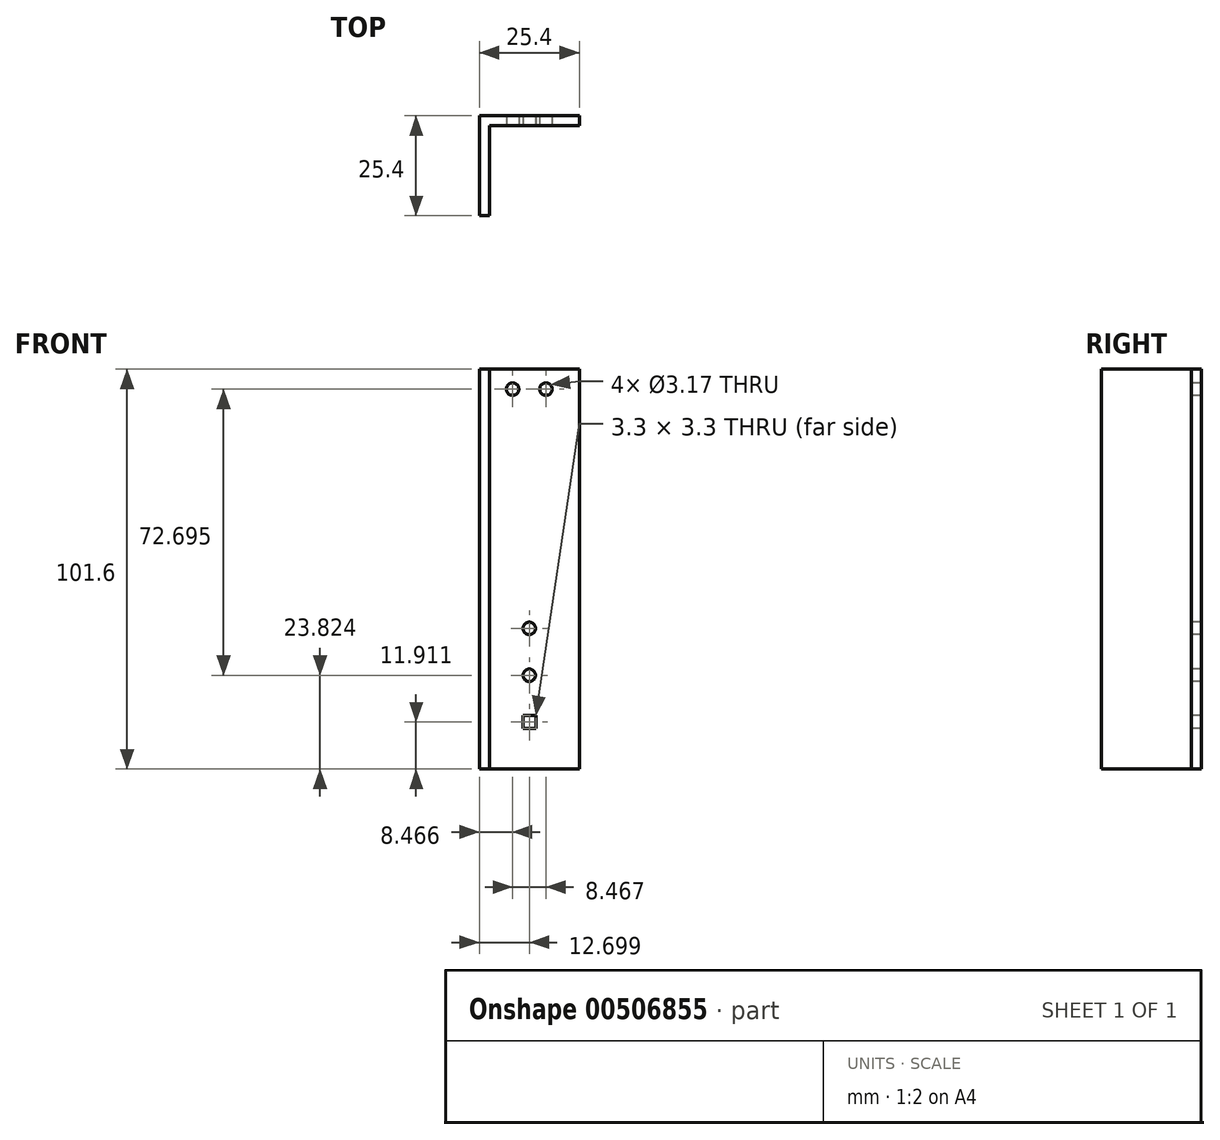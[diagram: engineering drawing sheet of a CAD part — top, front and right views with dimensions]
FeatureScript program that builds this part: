
annotation { "Feature Type Name" : "Feature", "Feature Type Description" : "" }
export const myFeature = defineFeature(function(context is Context, id is Id, definition is map)
    precondition{}
    {
        {
            var Q0;
            Q0=qCreatedBy(makeId("Front.planeOp"),FACE);
            var sketch = newSketch(context, id + "F0", { "sketchPlane" : qUnion([Q0])});
            skLineSegment(sketch, "E0.bottom", {"start": v(-30.83, 28.66) * mm, "end": v(-5.43, 28.66) * mm});
            skLineSegment(sketch, "E0.top", {"start": v(-30.83, -72.94) * mm, "end": v(-5.43, -72.94) * mm});
            skLineSegment(sketch, "E0.left", {"start": v(-30.83, 28.66) * mm, "end": v(-30.83, -72.94) * mm});
            skLineSegment(sketch, "E0.right", {"start": v(-5.43, 28.66) * mm, "end": v(-5.43, -72.94) * mm});
            skSolve(sketch);
        }
        {
            var Q0;
            Q0=makeQuery(id+"F0.imprint","IMPRINT",FACE,{"disambiguationData":[TD([[makeQuery(id+"F0.imprint","IMPRINT",EDGE,{"derivedFrom":sQuery(id+"F0.wireOp",EDGE,"E0.bottom")}),-1.0]])]});
            extrude(context, id + "F1", {"entities" : qUnion([Q0]), "depth" : 25.4 * mm, "offsetDistance" : 25.4 * mm});
        }
        {
            var Q0;
            Q0=makeQuery(id+"F1.opExtrude","SWEPT_FACE",FACE,{"disambiguationData":[OSD([sQuery(id+"F0.wireOp",EDGE,"E0.right")])]});
            var Q1;
            Q1=makeQuery(id+"F1.opExtrude","CAP_FACE",FACE,{"disambiguationData":[OSD([sQuery(id+"F0.wireOp",EDGE,"E0.bottom"),sQuery(id+"F0.wireOp",EDGE,"E0.top"),sQuery(id+"F0.wireOp",EDGE,"E0.left"),sQuery(id+"F0.wireOp",EDGE,"E0.right")])],"isStart":false});
            var Q2;
            Q2=makeQuery(id+"F1.opExtrude","SWEPT_FACE",FACE,{"disambiguationData":[OSD([sQuery(id+"F0.wireOp",EDGE,"E0.bottom")])]});
            var Q3;
            Q3=makeQuery(id+"F1.opExtrude","SWEPT_FACE",FACE,{"disambiguationData":[OSD([sQuery(id+"F0.wireOp",EDGE,"E0.top")])]});
            shell(context, id + "F2", {"entities" : qUnion([Q0, Q1, Q2, Q3]), "thickness" : 2.54 * mm});
        }
        {
            var Q0;
            Q0=makeQuery(id+"F2.opShell","OFFSET_FACE",FACE,{"disambiguationData":[OSD([sQuery(id+"F0.wireOp",EDGE,"E0.bottom"),sQuery(id+"F0.wireOp",EDGE,"E0.top"),sQuery(id+"F0.wireOp",EDGE,"E0.left"),sQuery(id+"F0.wireOp",EDGE,"E0.right")])]});
            var sketch = newSketch(context, id + "F3", { "sketchPlane" : qUnion([Q0])});
            skPoint(sketch, "E1", {"position": v(-22.36, 23.58) * mm});
            skPoint(sketch, "E2", {"position": v(-13.9, 23.58) * mm});
            skPoint(sketch, "E3", {"position": v(-18.13, -61.03) * mm});
            skPoint(sketch, "E4", {"position": v(-18.13, -49.12) * mm});
            skPoint(sketch, "E5", {"position": v(-18.13, -37.2) * mm});
            skLineSegment(sketch, "E6.bottom", {"start": v(-16.48, -62.68) * mm, "end": v(-19.78, -62.68) * mm});
            skLineSegment(sketch, "E6.top", {"start": v(-16.48, -59.38) * mm, "end": v(-19.78, -59.38) * mm});
            skLineSegment(sketch, "E6.left", {"start": v(-16.48, -62.68) * mm, "end": v(-16.48, -59.38) * mm});
            skLineSegment(sketch, "E6.right", {"start": v(-19.78, -62.68) * mm, "end": v(-19.78, -59.38) * mm});
            skSolve(sketch);
        }
        {
            var Q0;
            Q0=sQuery(id+"F3.wireOp",VERTEX,"E2");
            var Q1;
            Q1=sQuery(id+"F3.wireOp",VERTEX,"E1");
            var Q2;
            Q2=sQuery(id+"F3.wireOp",VERTEX,"E5");
            var Q3;
            Q3=sQuery(id+"F3.wireOp",VERTEX,"E4");
            var Q4;
            Q4=makeQuery(id+"F1.opExtrude","SWEPT_BODY",BODY,{"disambiguationData":[OSD([sQuery(id+"F0.wireOp",EDGE,"E0.bottom"),sQuery(id+"F0.wireOp",EDGE,"E0.top"),sQuery(id+"F0.wireOp",EDGE,"E0.left"),sQuery(id+"F0.wireOp",EDGE,"E0.right")])]});
            hole(context, id + "F4", {"style" : HoleStyle.SIMPLE, "endStyle" : HoleEndStyle.THROUGH, "holeDiameter" : 3.17 * mm, "majorDiameter" : 6.35 * mm, "isTappedThrough" : true, "tappedDepth" : 12.7 * mm, "tapClearance" : 3, "locations" : qUnion([Q0, Q1, Q2, Q3]), "scope" : qUnion([Q4])});
        }
        {
            var Q0;
            Q0=makeQuery(id+"F3.imprint","IMPRINT",FACE,{"disambiguationData":[TD([[makeQuery(id+"F3.imprint","IMPRINT",EDGE,{"derivedFrom":sQuery(id+"F3.wireOp",EDGE,"E6.bottom")}),-1.0]])]});
            extrude(context, id + "F5", {"entities" : qUnion([Q0]), "operationType" : NewBodyOperationType.REMOVE, "oppositeDirection" : true, "depth" : 5.84 * mm, "offsetDistance" : 25.4 * mm});
        }
    });
